FCSTD DOCUMENT  (FreeCAD 0.20R24992 (Git))
Label: joint-3
License: All rights reserved
LicenseURL: http://en.wikipedia.org/wiki/All_rights_reserved
objects: Sketcher::SketchObject×1, PartDesign::Body×1
note: 2 computed .brp shape members not serialized (recipe doc carries the construction recipe); baked Part::Feature solids carry a one-line shape summary decoded from their .brp

FEATURE [Sketcher::SketchObject] Sketch
  FullyConstrained = false
  MapMode = 5
  Placement = pos=(0,0,0) rot=(1,0,0;1.5708rad)
  Support = -> [XZ_Plane]
  sketch-geometry (7):
    g0: Circle CenterX=0 CenterY=0 CenterZ=0 NormalX=0 NormalY=0 NormalZ=1 AngleXU=0 Radius=2.15
    g1: Circle CenterX=0 CenterY=0 CenterZ=0 NormalX=0 NormalY=0 NormalZ=1 AngleXU=0 Radius=4.65
    g2: LineSegment StartX=3.72745 StartY=13.5482 StartZ=0 EndX=81.6052 EndY=13.5482 EndZ=0
    g3: LineSegment StartX=2.64831 StartY=33.1525 StartZ=0 EndX=80.526 EndY=33.1525 EndZ=0
    g4: LineSegment StartX=-4.65 StartY=-2.69315e-05 StartZ=0 EndX=-4.65 EndY=14.568 EndZ=0
    g5: LineSegment StartX=4.64647 StartY=0.181261 StartZ=0 EndX=4.64647 EndY=7.61793 EndZ=0
    g6: LineSegment StartX=4.64647 StartY=7.61793 StartZ=0 EndX=49.9392 EndY=7.61793 EndZ=0
  constraints (13):
    c: Coincident(g0,g-1)
    c: Coincident(g1,g0)
    c: Horizontal(g2)
    c: Horizontal(g3)
    c: Radius(g0) = 2.15
    c: Radius(g1) = 4.65
    c: PointOnObject(g4,g1)
    c: Vertical(g4)
    c: Tangent(g4,g1)
    c: PointOnObject(g5,g1)
    c: Coincident(g6,g5)
    c: Horizontal(g6)
    c: Vertical(g5)
FEATURE [PartDesign::Body] Body
  Group = -> [Sketch]
  Origin = -> Origin
